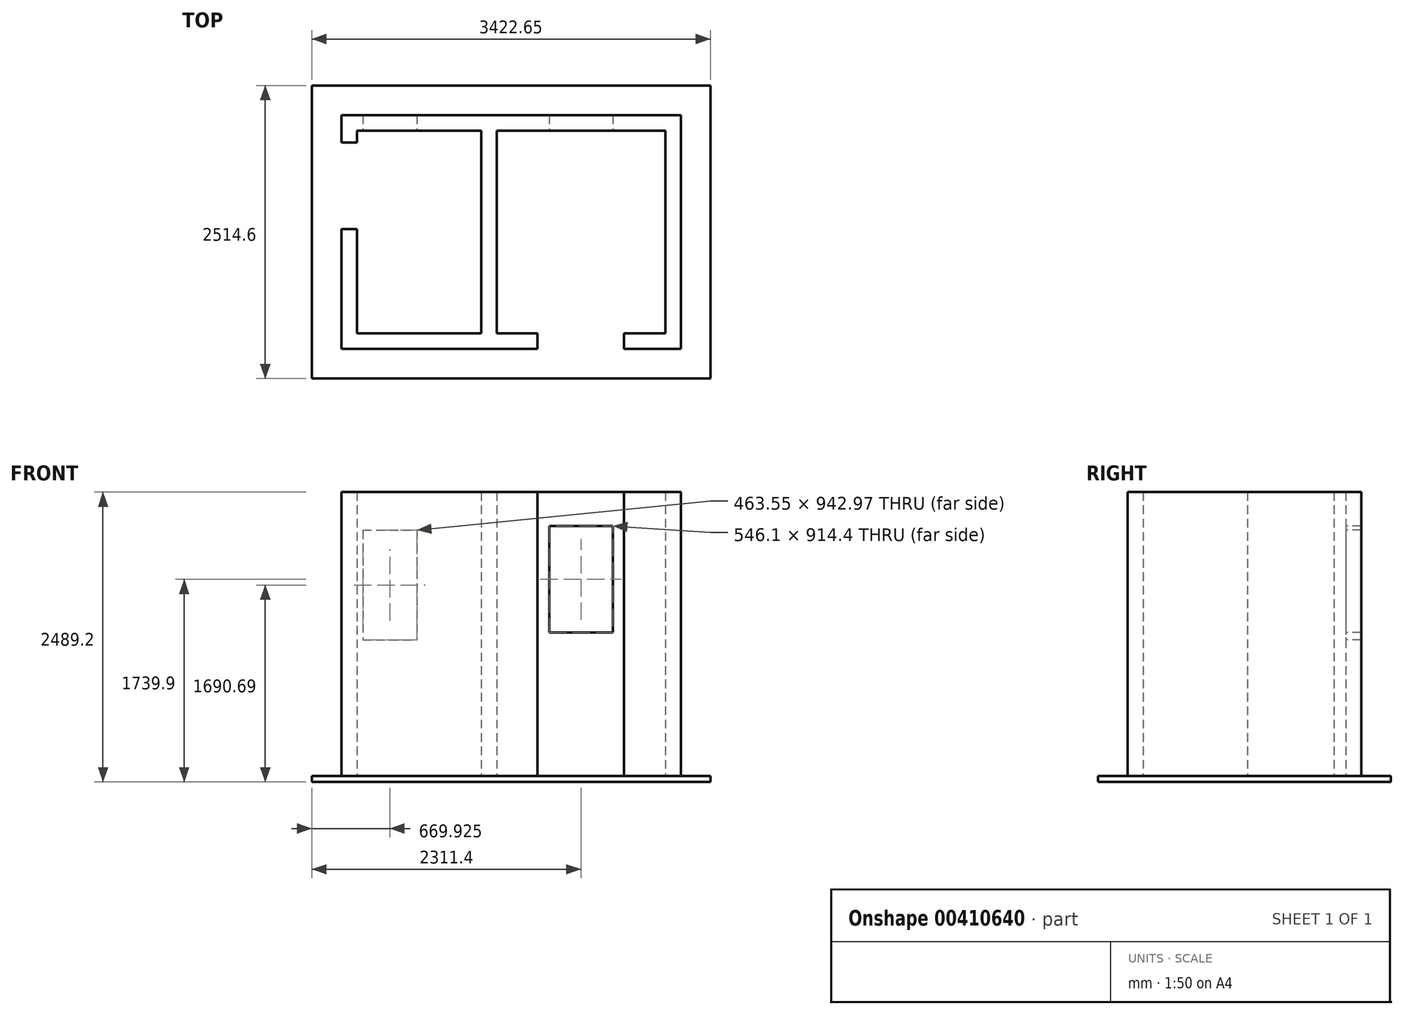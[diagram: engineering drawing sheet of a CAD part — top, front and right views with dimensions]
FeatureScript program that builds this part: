
annotation { "Feature Type Name" : "Feature", "Feature Type Description" : "" }
export const myFeature = defineFeature(function(context is Context, id is Id, definition is map)
    precondition{}
    {
        {
            var Q0;
            Q0=qCreatedBy(makeId("Top.planeOp"),FACE);
            var sketch = newSketch(context, id + "F0", { "sketchPlane" : qUnion([Q0])});
            skLineSegment(sketch, "E0.bottom", {"start": v(533.4, -869.95) * mm, "end": v(-533.4, -869.95) * mm});
            skLineSegment(sketch, "E0.top", {"start": v(533.4, 869.95) * mm, "end": v(-533.4, 869.95) * mm});
            skLineSegment(sketch, "E0.left", {"start": v(533.4, -869.95) * mm, "end": v(533.4, 869.95) * mm});
            skLineSegment(sketch, "E0.right", {"start": v(-533.4, -869.95) * mm, "end": v(-533.4, 869.95) * mm});
            skPoint(sketch, "E0.middle", {"position": v(0, 0) * mm});
            skLineSegment(sketch, "E1.bottom", {"start": v(666.75, 869.95) * mm, "end": v(2114.55, 869.95) * mm});
            skLineSegment(sketch, "E1.top", {"start": v(666.75, -869.95) * mm, "end": v(2114.55, -869.95) * mm});
            skLineSegment(sketch, "E1.left", {"start": v(666.75, 869.95) * mm, "end": v(666.75, -869.95) * mm});
            skLineSegment(sketch, "E1.right", {"start": v(2114.55, 869.95) * mm, "end": v(2114.55, -869.95) * mm});
            skLineSegment(sketch, "E2.0", {"start": v(2247.9, -1003.3) * mm, "end": v(-666.75, -1003.3) * mm});
            skLineSegment(sketch, "E2.1", {"start": v(-666.75, -1003.3) * mm, "end": v(-666.75, 1003.3) * mm});
            skLineSegment(sketch, "E2.2", {"start": v(2247.9, 1003.3) * mm, "end": v(-666.75, 1003.3) * mm});
            skLineSegment(sketch, "E3", {"start": v(2247.9, 1003.3) * mm, "end": v(2247.9, -1003.3) * mm});
            skLineSegment(sketch, "E4", {"start": v(1016, -869.95) * mm, "end": v(1016, -1003.3) * mm});
            skLineSegment(sketch, "E5", {"start": v(1758.95, -869.95) * mm, "end": v(1758.95, -1003.3) * mm});
            skLineSegment(sketch, "E6", {"start": v(-666.75, 768.35) * mm, "end": v(-533.4, 768.35) * mm});
            skLineSegment(sketch, "E7", {"start": v(-666.75, 25.4) * mm, "end": v(-533.4, 25.4) * mm});
            skSolve(sketch);
        }
        {
            var Q0;
            {var subQ8=sQuery(id+"F0.wireOp",EDGE,"E0.bottom");Q0=makeQuery(id+"F0.imprint","IMPRINT",FACE,{"disambiguationData":[TD([[makeQuery(id+"F0.imprint","IMPRINT",EDGE,{"derivedFrom":subQ8}),1.0]])]});}
            extrude(context, id + "F1", {"entities" : qUnion([Q0]), "depth" : 2438.4 * mm});
        }
        {
            var Q0;
            {var subQ0=sQuery(id+"F0.wireOp",EDGE,"E2.0");Q0=makeQuery(id+"F1.opExtrude","SWEPT_FACE",FACE,{"disambiguationData":[OSD([subQ0]),TDD([makeQuery(id+"F0.imprint","IMPRINT",EDGE,{"disambiguationData":[TD([[makeQuery(id+"F0.imprint","INTERSECT",VERTEX,{"derivedFrom":[subQ0,sQuery(id+"F0.wireOp",EDGE,"E2.1")]}),1.0]])],"derivedFrom":subQ0})])]});}
            var sketch = newSketch(context, id + "F2", { "sketchPlane" : qUnion([Q0])});
            skLineSegment(sketch, "E8.bottom", {"start": v(1016, 2438.4) * mm, "end": v(1758.95, 2438.4) * mm});
            skLineSegment(sketch, "E8.top", {"start": v(1016, 2032) * mm, "end": v(1758.95, 2032) * mm});
            skLineSegment(sketch, "E8.left", {"start": v(1016, 2438.4) * mm, "end": v(1016, 2032) * mm});
            skLineSegment(sketch, "E8.right", {"start": v(1758.95, 2438.4) * mm, "end": v(1758.95, 2032) * mm});
            skSolve(sketch);
        }
        {
            var Q0;
            {var subQ0=sQuery(id+"F0.wireOp",EDGE,"E2.1");Q0=makeQuery(id+"F1.opExtrude","SWEPT_FACE",FACE,{"disambiguationData":[OSD([subQ0]),TDD([makeQuery(id+"F0.imprint","IMPRINT",EDGE,{"disambiguationData":[TD([[makeQuery(id+"F0.imprint","INTERSECT",VERTEX,{"derivedFrom":[subQ0,sQuery(id+"F0.wireOp",EDGE,"E2.2")]}),1.0]])],"derivedFrom":subQ0})])]});}
            var sketch = newSketch(context, id + "F3", { "sketchPlane" : qUnion([Q0])});
            skLineSegment(sketch, "E9.bottom", {"start": v(-768.35, 2438.4) * mm, "end": v(-25.4, 2438.4) * mm});
            skLineSegment(sketch, "E9.top", {"start": v(-768.35, 2032) * mm, "end": v(-25.4, 2032) * mm});
            skLineSegment(sketch, "E9.left", {"start": v(-768.35, 2438.4) * mm, "end": v(-768.35, 2032) * mm});
            skLineSegment(sketch, "E9.right", {"start": v(-25.4, 2438.4) * mm, "end": v(-25.4, 2032) * mm});
            skSolve(sketch);
        }
        {
            var Q0;
            Q0=makeQuery(id+"F1.opExtrude","SWEPT_FACE",FACE,{"disambiguationData":[OSD([sQuery(id+"F0.wireOp",EDGE,"E0.top")])]});
            var sketch = newSketch(context, id + "F4", { "sketchPlane" : qUnion([Q0])});
            skLineSegment(sketch, "E10.bottom", {"start": v(-482.6, 2111.38) * mm, "end": v(-19.05, 2111.38) * mm});
            skLineSegment(sketch, "E10.top", {"start": v(-482.6, 1168.4) * mm, "end": v(-19.05, 1168.4) * mm});
            skLineSegment(sketch, "E10.left", {"start": v(-482.6, 2111.38) * mm, "end": v(-482.6, 1168.4) * mm});
            skLineSegment(sketch, "E10.right", {"start": v(-19.05, 2111.38) * mm, "end": v(-19.05, 1168.4) * mm});
            skLineSegment(sketch, "E11.bottom", {"start": v(1117.6, 2146.3) * mm, "end": v(1663.7, 2146.3) * mm});
            skLineSegment(sketch, "E11.top", {"start": v(1117.6, 1231.9) * mm, "end": v(1663.7, 1231.9) * mm});
            skLineSegment(sketch, "E11.left", {"start": v(1117.6, 2146.3) * mm, "end": v(1117.6, 1231.9) * mm});
            skLineSegment(sketch, "E11.right", {"start": v(1663.7, 2146.3) * mm, "end": v(1663.7, 1231.9) * mm});
            skSolve(sketch);
        }
        {
            var Q0;
            Q0 = qSketchRegion(id + "F4", true);
            extrude(context, id + "F5", {"entities" : qUnion([Q0]), "operationType" : NewBodyOperationType.REMOVE, "endBound" : BoundingType.THROUGH_ALL, "oppositeDirection" : true, "depth" : 25.4 * mm});
        }
        {
            var Q0;
            Q0=makeQuery(id+"F1.opExtrude","CAP_FACE",FACE,{"disambiguationData":[OSD([sQuery(id+"F0.wireOp",EDGE,"E0.bottom"),sQuery(id+"F0.wireOp",EDGE,"E0.top"),sQuery(id+"F0.wireOp",EDGE,"E0.left"),sQuery(id+"F0.wireOp",EDGE,"E0.right"),sQuery(id+"F0.wireOp",EDGE,"E1.bottom"),sQuery(id+"F0.wireOp",EDGE,"E1.top"),sQuery(id+"F0.wireOp",EDGE,"E1.left"),sQuery(id+"F0.wireOp",EDGE,"E1.right"),sQuery(id+"F0.wireOp",EDGE,"E2.0"),sQuery(id+"F0.wireOp",EDGE,"E2.1"),sQuery(id+"F0.wireOp",EDGE,"E2.2"),sQuery(id+"F0.wireOp",EDGE,"E3"),sQuery(id+"F0.wireOp",EDGE,"E4"),sQuery(id+"F0.wireOp",EDGE,"E5"),sQuery(id+"F0.wireOp",EDGE,"E6"),sQuery(id+"F0.wireOp",EDGE,"E7")])],"isStart":true});
            var sketch = newSketch(context, id + "F6", { "sketchPlane" : qUnion([Q0])});
            skLineSegment(sketch, "E12.2", {"start": v(2501.9, 1257.3) * mm, "end": v(-920.75, 1257.3) * mm});
            skLineSegment(sketch, "E12.3", {"start": v(2501.9, -1257.3) * mm, "end": v(2501.9, 1257.3) * mm});
            skLineSegment(sketch, "E12.4", {"start": v(-920.75, 1257.3) * mm, "end": v(-920.75, -1257.3) * mm});
            skLineSegment(sketch, "E12.7", {"start": v(2501.9, -1257.3) * mm, "end": v(-920.75, -1257.3) * mm});
            skSolve(sketch);
        }
        {
            var Q0;
            Q0 = qSketchRegion(id + "F6", true);
            extrude(context, id + "F7", {"entities" : qUnion([Q0]), "operationType" : NewBodyOperationType.ADD, "depth" : 50.8 * mm});
        }
    });
